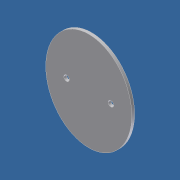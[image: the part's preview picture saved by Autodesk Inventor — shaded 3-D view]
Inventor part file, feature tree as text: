
AUTODESK INVENTOR PART (.ipt)
format: ipt  version: unknown  size: 174,592 bytes
history: native  units: in
note: dims shown in document units (in); Inventor stores cm internally (conversion verified against a paired STEP export)
features: sketch x2, extrude x1, hole x1
ambient origin geometry x8: Origin, YZ Plane, XZ Plane, XY Plane, X Axis, Y Axis, Z Axis, Center Point
bodies: Solid1 (feature_tree)
feature tree (4):
  extrude  "Extrusion1"  Depth=0.969in
  hole  "Hole1"  [1 undecoded]
  sketch  "Sketch1"  dims[d0=1.109in d1=0.969in]
  sketch  "Sketch2"  dims[d2=0.5in d3=1.0in d4=0.063in d5=0.0in d6=0.5in d7=0.5in d8=0.125in d9=0.75in d10=0.375in d11=0.25in d12=0.5635in d13=1.0in d14=0.8108in]
note: 1 required parameter value undecoded (feature->parameter linkage not recoverable at this tier; creation-order binding heuristic only, values carry confidence <= 0.55)
